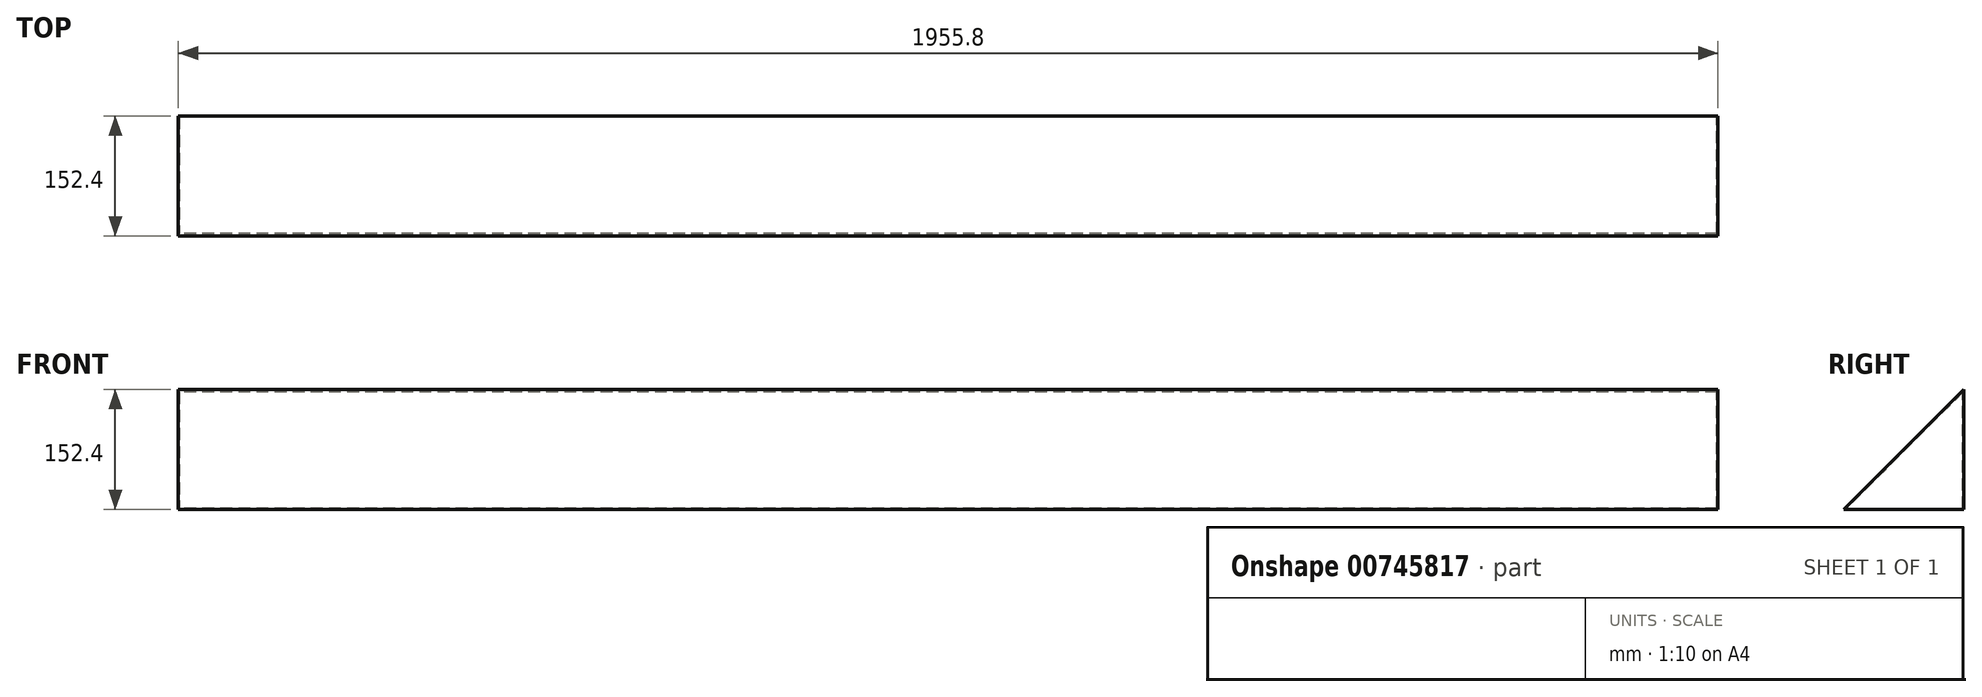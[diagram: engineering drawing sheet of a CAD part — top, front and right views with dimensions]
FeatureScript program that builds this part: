
annotation { "Feature Type Name" : "Feature", "Feature Type Description" : "" }
export const myFeature = defineFeature(function(context is Context, id is Id, definition is map)
    precondition{}
    {
        {
            var Q0;
            Q0=qCreatedBy(makeId("Right.planeOp"),FACE);
            var sketch = newSketch(context, id + "F0", { "sketchPlane" : qUnion([Q0])});
            skLineSegment(sketch, "E0", {"start": v(0, 0) * mm, "end": v(0, 152.4) * mm});
            skLineSegment(sketch, "E1", {"start": v(0, 152.4) * mm, "end": v(-152.4, 0) * mm});
            skLineSegment(sketch, "E2", {"start": v(-152.4, 0) * mm, "end": v(0, 0) * mm});
            skLineSegment(sketch, "E3.0", {"start": v(-1.27, 149.33) * mm, "end": v(-149.33, 1.27) * mm});
            skLineSegment(sketch, "E3.1", {"start": v(-1.27, 1.27) * mm, "end": v(-1.27, 149.33) * mm});
            skLineSegment(sketch, "E3.2", {"start": v(-149.33, 1.27) * mm, "end": v(-1.27, 1.27) * mm});
            skSolve(sketch);
        }
        {
            var Q0;
            Q0=makeQuery(id+"F0.imprint","IMPRINT",FACE,{"disambiguationData":[TD([[makeQuery(id+"F0.imprint","IMPRINT",EDGE,{"derivedFrom":sQuery(id+"F0.wireOp",EDGE,"E0")}),1.0]])]});
            extrude(context, id + "F1", {"entities" : qUnion([Q0]), "depth" : 1955.8 * mm, "offsetDistance" : 25.4 * mm});
        }
        {
            var Q0;
            Q0=makeQuery(id+"F1.opExtrude","CAP_FACE",FACE,{"disambiguationData":[OSD([sQuery(id+"F0.wireOp",EDGE,"E0"),sQuery(id+"F0.wireOp",EDGE,"E1"),sQuery(id+"F0.wireOp",EDGE,"E2"),sQuery(id+"F0.wireOp",EDGE,"E3.0"),sQuery(id+"F0.wireOp",EDGE,"E3.1"),sQuery(id+"F0.wireOp",EDGE,"E3.2")])],"isStart":true});
            var sketch = newSketch(context, id + "F2", { "sketchPlane" : qUnion([Q0])});
            skLineSegment(sketch, "E4.0", {"start": v(1.27, 1.27) * mm, "end": v(1.27, 149.33) * mm});
            skLineSegment(sketch, "E5.0", {"start": v(1.27, 149.33) * mm, "end": v(149.33, 1.27) * mm});
            skLineSegment(sketch, "E6.0", {"start": v(149.33, 1.27) * mm, "end": v(1.27, 1.27) * mm});
            skSolve(sketch);
        }
        {
            var Q0;
            Q0 = qSketchRegion(id + "F2", true);
            extrude(context, id + "F3", {"entities" : qUnion([Q0]), "operationType" : NewBodyOperationType.ADD, "oppositeDirection" : true, "depth" : 1.27 * mm, "offsetDistance" : 25.4 * mm});
        }
        {
            var Q0;
            Q0=makeQuery(id+"F1.opExtrude","CAP_FACE",FACE,{"disambiguationData":[OSD([sQuery(id+"F0.wireOp",EDGE,"E0"),sQuery(id+"F0.wireOp",EDGE,"E1"),sQuery(id+"F0.wireOp",EDGE,"E2"),sQuery(id+"F0.wireOp",EDGE,"E3.0"),sQuery(id+"F0.wireOp",EDGE,"E3.1"),sQuery(id+"F0.wireOp",EDGE,"E3.2")])],"isStart":false});
            var sketch = newSketch(context, id + "F4", { "sketchPlane" : qUnion([Q0])});
            skLineSegment(sketch, "E7.0", {"start": v(-1.27, 1.27) * mm, "end": v(-1.27, 149.33) * mm});
            skLineSegment(sketch, "E8.0", {"start": v(-1.27, 149.33) * mm, "end": v(-149.33, 1.27) * mm});
            skLineSegment(sketch, "E9.0", {"start": v(-149.33, 1.27) * mm, "end": v(-1.27, 1.27) * mm});
            skSolve(sketch);
        }
        {
            var Q0;
            Q0 = qSketchRegion(id + "F4", true);
            extrude(context, id + "F5", {"entities" : qUnion([Q0]), "operationType" : NewBodyOperationType.ADD, "oppositeDirection" : true, "depth" : 1.27 * mm, "offsetDistance" : 25.4 * mm});
        }
    });
